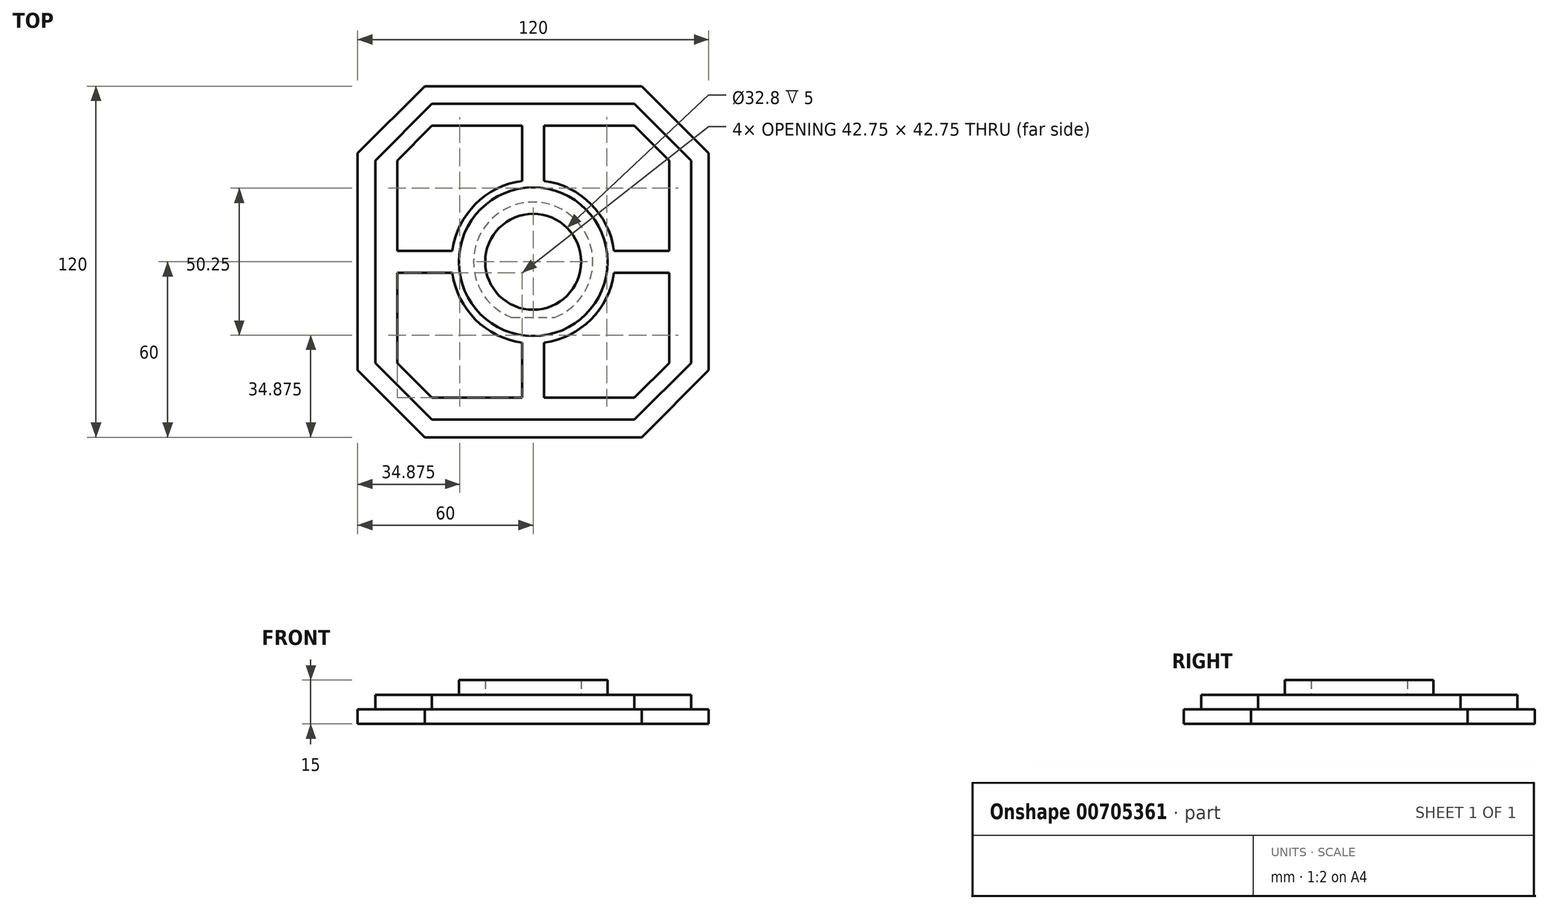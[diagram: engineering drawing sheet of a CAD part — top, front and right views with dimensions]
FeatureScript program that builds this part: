
annotation { "Feature Type Name" : "Feature", "Feature Type Description" : "" }
export const myFeature = defineFeature(function(context is Context, id is Id, definition is map)
    precondition{}
    {
        {
            assignVariable(context, id + "F0", {"name" : "skirt", "anyValue" : 5 * mm});
        }
        {
            var Q0;
            Q0=qCreatedBy(makeId("Top.planeOp"),FACE);
            var sketch = newSketch(context, id + "F1", { "sketchPlane" : qUnion([Q0])});
            skLineSegment(sketch, "E0.bottom", {"start": v(-55, 55) * mm, "end": v(55, 55) * mm});
            skLineSegment(sketch, "E0.top", {"start": v(-55, -55) * mm, "end": v(55, -55) * mm});
            skLineSegment(sketch, "E0.left", {"start": v(-55, 55) * mm, "end": v(-55, -55) * mm});
            skLineSegment(sketch, "E0.right", {"start": v(55, 55) * mm, "end": v(55, -55) * mm});
            skPoint(sketch, "E0.middle", {"position": v(0, 0) * mm});
            skCircle(sketch, "E1", {"center": v(0, 0) * mm, "radius": 19.4 * mm});
            skCircle(sketch, "E2", {"center": v(0, 0) * mm, "radius": 15.4 * mm});
            skLineSegment(sketch, "E3", {"start": v(-55, -35) * mm, "end": v(-35, -55) * mm});
            skLineSegment(sketch, "E4", {"start": v(-35, 55) * mm, "end": v(-55, 35) * mm});
            skLineSegment(sketch, "E5", {"start": v(35, 55) * mm, "end": v(55, 35) * mm});
            skLineSegment(sketch, "E6", {"start": v(55, -35) * mm, "end": v(35, -55) * mm});
            skLineSegment(sketch, "E7.0", {"start": v(-60, 60) * mm, "end": v(-60, -60) * mm});
            skLineSegment(sketch, "E7.1", {"start": v(-60, 60) * mm, "end": v(60, 60) * mm});
            skLineSegment(sketch, "E7.2", {"start": v(60, 60) * mm, "end": v(60, -60) * mm});
            skLineSegment(sketch, "E7.3", {"start": v(-60, -60) * mm, "end": v(60, -60) * mm});
            skLineSegment(sketch, "E8", {"start": v(-60, -37.07) * mm, "end": v(-37.07, -60) * mm});
            skLineSegment(sketch, "E9", {"start": v(60, -37.07) * mm, "end": v(37.07, -60) * mm});
            skLineSegment(sketch, "E10", {"start": v(60, 37.07) * mm, "end": v(37.07, 60) * mm});
            skLineSegment(sketch, "E11", {"start": v(-37.07, 60) * mm, "end": v(-60, 37.07) * mm});
            skCircle(sketch, "E12", {"center": v(0, 0) * mm, "radius": 20.4 * mm});
            skLineSegment(sketch, "E13.0", {"start": v(-54, 54) * mm, "end": v(54, 54) * mm});
            skLineSegment(sketch, "E13.1", {"start": v(-54, 54) * mm, "end": v(-54, -54) * mm});
            skLineSegment(sketch, "E13.2", {"start": v(-54, -54) * mm, "end": v(54, -54) * mm});
            skLineSegment(sketch, "E13.3", {"start": v(54, 54) * mm, "end": v(54, -54) * mm});
            skLineSegment(sketch, "E14", {"start": v(-34.59, 54) * mm, "end": v(-54, 34.59) * mm});
            skLineSegment(sketch, "E15", {"start": v(34.59, 54) * mm, "end": v(54, 34.59) * mm});
            skLineSegment(sketch, "E16", {"start": v(54, -34.59) * mm, "end": v(34.59, -54) * mm});
            skLineSegment(sketch, "E17", {"start": v(-34.59, -54) * mm, "end": v(-54, -34.59) * mm});
            skCircle(sketch, "E18", {"center": v(0, 0) * mm, "radius": 16.4 * mm});
            skLineSegment(sketch, "E19", {"start": v(0, 16.4) * mm, "end": v(0, 0) * mm, "construction": true});
            skLineSegment(sketch, "E20", {"start": v(-7.43, -19) * mm, "end": v(7.43, -19) * mm});
            skCircle(sketch, "E21", {"center": v(0, 0) * mm, "radius": 27.9 * mm});
            skLineSegment(sketch, "E22", {"start": v(-46.5, -34.59) * mm, "end": v(-46.5, 34.59) * mm});
            skLineSegment(sketch, "E23", {"start": v(-34.59, 46.5) * mm, "end": v(34.59, 46.5) * mm});
            skLineSegment(sketch, "E24", {"start": v(46.5, 34.59) * mm, "end": v(46.5, -34.59) * mm});
            skLineSegment(sketch, "E25", {"start": v(-34.59, -46.5) * mm, "end": v(34.59, -46.5) * mm});
            skLineSegment(sketch, "E26", {"start": v(46.5, -34.59) * mm, "end": v(34.59, -46.5) * mm});
            skLineSegment(sketch, "E27", {"start": v(46.5, 34.59) * mm, "end": v(34.59, 46.5) * mm});
            skLineSegment(sketch, "E28", {"start": v(-34.59, 46.5) * mm, "end": v(-46.5, 34.59) * mm});
            skLineSegment(sketch, "E29", {"start": v(-46.5, -34.59) * mm, "end": v(-34.59, -46.5) * mm});
            skLineSegment(sketch, "E30", {"start": v(0, -27.9) * mm, "end": v(0, -46.5) * mm, "construction": true});
            skLineSegment(sketch, "E31", {"start": v(27.9, 0) * mm, "end": v(46.5, 0) * mm, "construction": true});
            skLineSegment(sketch, "E32", {"start": v(0, 27.9) * mm, "end": v(0, 46.5) * mm, "construction": true});
            skLineSegment(sketch, "E33", {"start": v(-27.9, 0) * mm, "end": v(-46.5, 0) * mm, "construction": true});
            skLineSegment(sketch, "E34", {"start": v(-3.75, -27.65) * mm, "end": v(-3.75, -46.5) * mm});
            skLineSegment(sketch, "E35", {"start": v(3.75, -27.65) * mm, "end": v(3.75, -46.5) * mm});
            skLineSegment(sketch, "E36", {"start": v(-3.75, -37.2) * mm, "end": v(3.75, -37.2) * mm, "construction": true});
            skPoint(sketch, "E37", {"position": v(0, -37.2) * mm});
            skLineSegment(sketch, "E38", {"start": v(-27.65, 3.75) * mm, "end": v(-46.5, 3.75) * mm});
            skLineSegment(sketch, "E39", {"start": v(-46.5, -3.75) * mm, "end": v(-27.65, -3.75) * mm});
            skLineSegment(sketch, "E40", {"start": v(-37.2, 3.75) * mm, "end": v(-37.2, -3.75) * mm, "construction": true});
            skPoint(sketch, "E41", {"position": v(-37.2, 0) * mm});
            skLineSegment(sketch, "E42", {"start": v(27.65, 3.75) * mm, "end": v(46.5, 3.75) * mm});
            skLineSegment(sketch, "E43", {"start": v(27.65, -3.75) * mm, "end": v(46.5, -3.75) * mm});
            skLineSegment(sketch, "E44", {"start": v(3.75, 27.65) * mm, "end": v(3.75, 46.5) * mm});
            skLineSegment(sketch, "E45", {"start": v(-3.75, 27.65) * mm, "end": v(-3.75, 46.5) * mm});
            skSolve(sketch);
        }
        {
            var Q0;
            {var subQ5=sQuery(id+"F1.wireOp",EDGE,"E0.bottom");var subQ9=makeQuery(id+"F1.imprint","INTERSECT",VERTEX,{"derivedFrom":[subQ5,sQuery(id+"F1.wireOp",EDGE,"E4")]});Q0=makeQuery(id+"F1.imprint","IMPRINT",FACE,{"disambiguationData":[TD([[makeQuery(id+"F1.imprint","IMPRINT",EDGE,{"disambiguationData":[TD([[subQ9,1.0]])],"derivedFrom":subQ5}),1.0]])]});}
            var Q1;
            {var subQ0=sQuery(id+"F1.wireOp",EDGE,"E4");Q1=makeQuery(id+"F1.imprint","IMPRINT",FACE,{"disambiguationData":[TD([[makeQuery(id+"F1.imprint","IMPRINT",EDGE,{"derivedFrom":subQ0}),-1.0]])]});}
            var Q2;
            {var subQ0=sQuery(id+"F1.wireOp",EDGE,"E0.left");var subQ9=makeQuery(id+"F1.imprint","INTERSECT",VERTEX,{"derivedFrom":[subQ0,sQuery(id+"F1.wireOp",EDGE,"E4")]});Q2=makeQuery(id+"F1.imprint","IMPRINT",FACE,{"disambiguationData":[TD([[makeQuery(id+"F1.imprint","IMPRINT",EDGE,{"disambiguationData":[TD([[subQ9,1.0]])],"derivedFrom":subQ0}),-1.0]])]});}
            var Q3;
            {var subQ3=sQuery(id+"F1.wireOp",EDGE,"E3");Q3=makeQuery(id+"F1.imprint","IMPRINT",FACE,{"disambiguationData":[TD([[makeQuery(id+"F1.imprint","IMPRINT",EDGE,{"derivedFrom":subQ3}),1.0]])]});}
            var Q4;
            {var subQ0=sQuery(id+"F1.wireOp",EDGE,"E3");Q4=makeQuery(id+"F1.imprint","IMPRINT",FACE,{"disambiguationData":[TD([[makeQuery(id+"F1.imprint","IMPRINT",EDGE,{"derivedFrom":subQ0}),-1.0]])]});}
            var Q5;
            {var subQ0=sQuery(id+"F1.wireOp",EDGE,"E0.top");var subQ4=makeQuery(id+"F1.imprint","INTERSECT",VERTEX,{"derivedFrom":[subQ0,sQuery(id+"F1.wireOp",EDGE,"E3")]});Q5=makeQuery(id+"F1.imprint","IMPRINT",FACE,{"disambiguationData":[TD([[makeQuery(id+"F1.imprint","IMPRINT",EDGE,{"disambiguationData":[TD([[subQ4,1.0]])],"derivedFrom":subQ0}),-1.0]])]});}
            var Q6;
            {var subQ0=sQuery(id+"F1.wireOp",EDGE,"E6");Q6=makeQuery(id+"F1.imprint","IMPRINT",FACE,{"disambiguationData":[TD([[makeQuery(id+"F1.imprint","IMPRINT",EDGE,{"derivedFrom":subQ0}),1.0]])]});}
            var Q7;
            {var subQ5=sQuery(id+"F1.wireOp",EDGE,"E0.right");var subQ9=makeQuery(id+"F1.imprint","INTERSECT",VERTEX,{"derivedFrom":[subQ5,sQuery(id+"F1.wireOp",EDGE,"E5")]});Q7=makeQuery(id+"F1.imprint","IMPRINT",FACE,{"disambiguationData":[TD([[makeQuery(id+"F1.imprint","IMPRINT",EDGE,{"disambiguationData":[TD([[subQ9,1.0]])],"derivedFrom":subQ5}),1.0]])]});}
            var Q8;
            {var subQ0=sQuery(id+"F1.wireOp",EDGE,"E5");Q8=makeQuery(id+"F1.imprint","IMPRINT",FACE,{"disambiguationData":[TD([[makeQuery(id+"F1.imprint","IMPRINT",EDGE,{"derivedFrom":subQ0}),1.0]])]});}
            var Q9;
            Q9=makeQuery(id+"F1.imprint","IMPRINT",FACE,{"disambiguationData":[TD([[makeQuery(id+"F1.imprint","IMPRINT",EDGE,{"derivedFrom":sQuery(id+"F1.wireOp",EDGE,"E12")}),-1.0]])]});
            var Q10;
            {var subQ2=sQuery(id+"F1.wireOp",EDGE,"E4");var subQ4=sQuery(id+"F1.wireOp",EDGE,"E0.bottom");var subQ5=makeQuery(id+"F1.imprint","INTERSECT",VERTEX,{"derivedFrom":[subQ4,subQ2]});Q10=makeQuery(id+"F1.imprint","IMPRINT",FACE,{"disambiguationData":[TD([[makeQuery(id+"F1.imprint","IMPRINT",EDGE,{"disambiguationData":[TD([[subQ5,-1.0]])],"derivedFrom":subQ4}),-1.0]])]});}
            var Q11;
            {var subQ5=sQuery(id+"F1.wireOp",EDGE,"E14");Q11=makeQuery(id+"F1.imprint","IMPRINT",FACE,{"disambiguationData":[TD([[makeQuery(id+"F1.imprint","IMPRINT",EDGE,{"derivedFrom":subQ5}),-1.0]])]});}
            var Q12;
            {var subQ4=sQuery(id+"F1.wireOp",EDGE,"E0.left");var subQ6=sQuery(id+"F1.wireOp",EDGE,"E3");var subQ7=makeQuery(id+"F1.imprint","INTERSECT",VERTEX,{"derivedFrom":[subQ4,subQ6]});Q12=makeQuery(id+"F1.imprint","IMPRINT",FACE,{"disambiguationData":[TD([[makeQuery(id+"F1.imprint","IMPRINT",EDGE,{"disambiguationData":[TD([[subQ7,1.0]])],"derivedFrom":subQ4}),1.0]])]});}
            var Q13;
            {var subQ2=sQuery(id+"F1.wireOp",EDGE,"E3");var subQ5=sQuery(id+"F1.wireOp",EDGE,"E0.top");var subQ8=makeQuery(id+"F1.imprint","INTERSECT",VERTEX,{"derivedFrom":[subQ5,subQ2]});Q13=makeQuery(id+"F1.imprint","IMPRINT",FACE,{"disambiguationData":[TD([[makeQuery(id+"F1.imprint","IMPRINT",EDGE,{"disambiguationData":[TD([[subQ8,-1.0]])],"derivedFrom":subQ5}),1.0]])]});}
            var Q14;
            {var subQ5=sQuery(id+"F1.wireOp",EDGE,"E16");Q14=makeQuery(id+"F1.imprint","IMPRINT",FACE,{"disambiguationData":[TD([[makeQuery(id+"F1.imprint","IMPRINT",EDGE,{"derivedFrom":subQ5}),1.0]])]});}
            var Q15;
            {var subQ1=sQuery(id+"F1.wireOp",EDGE,"E0.right");var subQ6=sQuery(id+"F1.wireOp",EDGE,"E5");var subQ8=makeQuery(id+"F1.imprint","INTERSECT",VERTEX,{"derivedFrom":[subQ1,subQ6]});Q15=makeQuery(id+"F1.imprint","IMPRINT",FACE,{"disambiguationData":[TD([[makeQuery(id+"F1.imprint","IMPRINT",EDGE,{"disambiguationData":[TD([[subQ8,-1.0]])],"derivedFrom":subQ1}),-1.0]])]});}
            var Q16;
            {var subQ5=sQuery(id+"F1.wireOp",EDGE,"E15");Q16=makeQuery(id+"F1.imprint","IMPRINT",FACE,{"disambiguationData":[TD([[makeQuery(id+"F1.imprint","IMPRINT",EDGE,{"derivedFrom":subQ5}),1.0]])]});}
            var Q17;
            {var subQ0=sQuery(id+"F1.wireOp",EDGE,"E20");var subQ1=sQuery(id+"F1.wireOp",EDGE,"E1");var subQ2=makeQuery(id+"F1.imprint","INTERSECT",VERTEX,{"disambiguationData":[OD(0.0)],"derivedFrom":[subQ1,subQ0]});Q17=makeQuery(id+"F1.imprint","IMPRINT",FACE,{"disambiguationData":[TD([[makeQuery(id+"F1.imprint","IMPRINT",EDGE,{"disambiguationData":[TD([[subQ2,-1.0]])],"derivedFrom":subQ1}),-1.0]])]});}
            var Q18;
            {var subQ0=sQuery(id+"F1.wireOp",EDGE,"E20");var subQ1=sQuery(id+"F1.wireOp",EDGE,"E1");var subQ2=makeQuery(id+"F1.imprint","INTERSECT",VERTEX,{"disambiguationData":[OD(0.0)],"derivedFrom":[subQ1,subQ0]});Q18=makeQuery(id+"F1.imprint","IMPRINT",FACE,{"disambiguationData":[TD([[makeQuery(id+"F1.imprint","IMPRINT",EDGE,{"disambiguationData":[TD([[subQ2,-1.0]])],"derivedFrom":subQ1}),1.0]])]});}
            var Q19;
            {var subQ1=sQuery(id+"F1.wireOp",EDGE,"E14");Q19=makeQuery(id+"F1.imprint","IMPRINT",FACE,{"disambiguationData":[TD([[makeQuery(id+"F1.imprint","IMPRINT",EDGE,{"derivedFrom":subQ1}),1.0]])]});}
            var Q20;
            {var subQ0=sQuery(id+"F1.wireOp",EDGE,"E42");Q20=makeQuery(id+"F1.imprint","IMPRINT",FACE,{"disambiguationData":[TD([[makeQuery(id+"F1.imprint","IMPRINT",EDGE,{"derivedFrom":subQ0}),-1.0]])]});}
            var Q21;
            {var subQ0=sQuery(id+"F1.wireOp",EDGE,"E44");Q21=makeQuery(id+"F1.imprint","IMPRINT",FACE,{"disambiguationData":[TD([[makeQuery(id+"F1.imprint","IMPRINT",EDGE,{"derivedFrom":subQ0}),1.0]])]});}
            var Q22;
            {var subQ0=sQuery(id+"F1.wireOp",EDGE,"E38");Q22=makeQuery(id+"F1.imprint","IMPRINT",FACE,{"disambiguationData":[TD([[makeQuery(id+"F1.imprint","IMPRINT",EDGE,{"derivedFrom":subQ0}),1.0]])]});}
            var Q23;
            {var subQ0=sQuery(id+"F1.wireOp",EDGE,"E34");Q23=makeQuery(id+"F1.imprint","IMPRINT",FACE,{"disambiguationData":[TD([[makeQuery(id+"F1.imprint","IMPRINT",EDGE,{"derivedFrom":subQ0}),1.0]])]});}
            extrude(context, id + "F2", {"entities" : qUnion([Q0, Q1, Q2, Q3, Q4, Q5, Q6, Q7, Q8, Q9, Q10, Q11, Q12, Q13, Q14, Q15, Q16, Q17, Q18, Q19, Q20, Q21, Q22, Q23]), "oppositeDirection" : true, "depth" : getVariable(context, 'skirt'), "offsetDistance" : 25 * mm});
        }
        {
            var Q0;
            Q0=makeQuery(id+"F1.imprint","IMPRINT",FACE,{"disambiguationData":[TD([[makeQuery(id+"F1.imprint","IMPRINT",EDGE,{"derivedFrom":sQuery(id+"F1.wireOp",EDGE,"E12")}),-1.0]])]});
            var Q1;
            {var subQ0=sQuery(id+"F1.wireOp",EDGE,"E20");var subQ1=sQuery(id+"F1.wireOp",EDGE,"E1");var subQ2=makeQuery(id+"F1.imprint","INTERSECT",VERTEX,{"disambiguationData":[OD(0.0)],"derivedFrom":[subQ1,subQ0]});Q1=makeQuery(id+"F1.imprint","IMPRINT",FACE,{"disambiguationData":[TD([[makeQuery(id+"F1.imprint","IMPRINT",EDGE,{"disambiguationData":[TD([[subQ2,-1.0]])],"derivedFrom":subQ1}),-1.0]])]});}
            var Q2;
            {var subQ0=sQuery(id+"F1.wireOp",EDGE,"E20");var subQ1=sQuery(id+"F1.wireOp",EDGE,"E1");var subQ2=makeQuery(id+"F1.imprint","INTERSECT",VERTEX,{"disambiguationData":[OD(0.0)],"derivedFrom":[subQ1,subQ0]});Q2=makeQuery(id+"F1.imprint","IMPRINT",FACE,{"disambiguationData":[TD([[makeQuery(id+"F1.imprint","IMPRINT",EDGE,{"disambiguationData":[TD([[subQ2,-1.0]])],"derivedFrom":subQ1}),1.0]])]});}
            var Q3;
            {var subQ1=sQuery(id+"F1.wireOp",EDGE,"E14");Q3=makeQuery(id+"F1.imprint","IMPRINT",FACE,{"disambiguationData":[TD([[makeQuery(id+"F1.imprint","IMPRINT",EDGE,{"derivedFrom":subQ1}),1.0]])]});}
            var Q4;
            {var subQ0=sQuery(id+"F1.wireOp",EDGE,"E34");Q4=makeQuery(id+"F1.imprint","IMPRINT",FACE,{"disambiguationData":[TD([[makeQuery(id+"F1.imprint","IMPRINT",EDGE,{"derivedFrom":subQ0}),1.0]])]});}
            var Q5;
            {var subQ0=sQuery(id+"F1.wireOp",EDGE,"E38");Q5=makeQuery(id+"F1.imprint","IMPRINT",FACE,{"disambiguationData":[TD([[makeQuery(id+"F1.imprint","IMPRINT",EDGE,{"derivedFrom":subQ0}),1.0]])]});}
            var Q6;
            {var subQ0=sQuery(id+"F1.wireOp",EDGE,"E42");Q6=makeQuery(id+"F1.imprint","IMPRINT",FACE,{"disambiguationData":[TD([[makeQuery(id+"F1.imprint","IMPRINT",EDGE,{"derivedFrom":subQ0}),-1.0]])]});}
            var Q7;
            {var subQ0=sQuery(id+"F1.wireOp",EDGE,"E44");Q7=makeQuery(id+"F1.imprint","IMPRINT",FACE,{"disambiguationData":[TD([[makeQuery(id+"F1.imprint","IMPRINT",EDGE,{"derivedFrom":subQ0}),1.0]])]});}
            extrude(context, id + "F3", {"entities" : qUnion([Q0, Q1, Q2, Q3, Q4, Q5, Q6, Q7]), "operationType" : NewBodyOperationType.ADD, "depth" : getVariable(context, 'skirt'), "offsetDistance" : 25 * mm});
        }
        {
            var Q0;
            Q0=makeQuery(id+"F3.opExtrude","CAP_FACE",FACE,{"disambiguationData":[OSD([sQuery(id+"F1.wireOp",EDGE,"E12"),sQuery(id+"F1.wireOp",EDGE,"E13.0"),sQuery(id+"F1.wireOp",EDGE,"E13.1"),sQuery(id+"F1.wireOp",EDGE,"E13.2"),sQuery(id+"F1.wireOp",EDGE,"E13.3"),sQuery(id+"F1.wireOp",EDGE,"E14"),sQuery(id+"F1.wireOp",EDGE,"E15"),sQuery(id+"F1.wireOp",EDGE,"E16"),sQuery(id+"F1.wireOp",EDGE,"E17")])],"isStart":false});
            var sketch = newSketch(context, id + "F4", { "sketchPlane" : qUnion([Q0])});
            skCircle(sketch, "E46", {"center": v(0, 0) * mm, "radius": 25.4 * mm});
            skCircle(sketch, "E47", {"center": v(0, 0) * mm, "radius": 16.4 * mm});
            skLineSegment(sketch, "E48", {"start": v(0, 0) * mm, "end": v(16.4, 0) * mm, "construction": true});
            skSolve(sketch);
        }
        {
            var Q0;
            Q0=makeQuery(id+"F4.imprint","IMPRINT",FACE,{"disambiguationData":[TD([[makeQuery(id+"F4.imprint","IMPRINT",EDGE,{"derivedFrom":sQuery(id+"F4.wireOp",EDGE,"E46")}),1.0]])]});
            var Q1;
            Q1=makeQuery(id+"F4.imprint","IMPRINT",FACE,{"disambiguationData":[TD([[makeQuery(id+"F4.imprint","IMPRINT",EDGE,{"derivedFrom":sQuery(id+"F4.wireOp",EDGE,"E47")}),-1.0]])]});
            extrude(context, id + "F5", {"entities" : qUnion([Q0, Q1]), "operationType" : NewBodyOperationType.ADD, "depth" : getVariable(context, 'skirt'), "offsetDistance" : 25 * mm});
        }
    });
